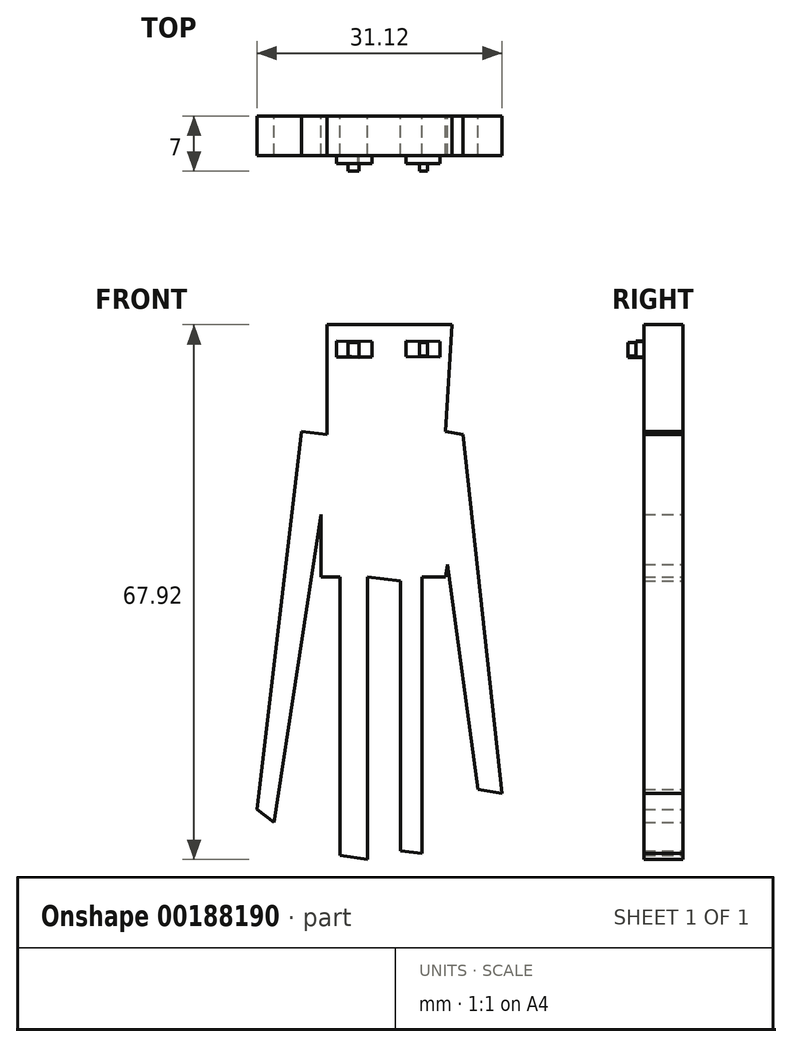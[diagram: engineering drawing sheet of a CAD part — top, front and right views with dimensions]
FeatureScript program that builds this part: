
annotation { "Feature Type Name" : "Feature", "Feature Type Description" : "" }
export const myFeature = defineFeature(function(context is Context, id is Id, definition is map)
    precondition{}
    {
        {
            var Q0;
            Q0=qCreatedBy(makeId("Front.planeOp"),FACE);
            var sketch = newSketch(context, id + "F0", { "sketchPlane" : qUnion([Q0])});
            skLineSegment(sketch, "E0", {"start": v(-12.61, 8.24) * mm, "end": v(-18.23, -39.76) * mm});
            skLineSegment(sketch, "E1", {"start": v(-18.23, -39.76) * mm, "end": v(-16.06, -41.4) * mm});
            skLineSegment(sketch, "E2", {"start": v(-16.06, -41.4) * mm, "end": v(-10.08, -2.27) * mm});
            skLineSegment(sketch, "E3", {"start": v(-10.08, -2.27) * mm, "end": v(-10.08, -10.24) * mm});
            skLineSegment(sketch, "E4", {"start": v(-10.08, -10.24) * mm, "end": v(5.68, -10.24) * mm});
            skLineSegment(sketch, "E5", {"start": v(5.68, -10.24) * mm, "end": v(5.93, -8.62) * mm});
            skLineSegment(sketch, "E6", {"start": v(5.93, -8.62) * mm, "end": v(9.85, -37.23) * mm});
            skLineSegment(sketch, "E7", {"start": v(9.85, -37.23) * mm, "end": v(12.9, -37.7) * mm});
            skLineSegment(sketch, "E8", {"start": v(12.9, -37.7) * mm, "end": v(7.96, 7.9) * mm});
            skLineSegment(sketch, "E9", {"start": v(7.96, 7.9) * mm, "end": v(5.68, 8.24) * mm});
            skLineSegment(sketch, "E10", {"start": v(-9.35, 21.83) * mm, "end": v(-9.35, 7.88) * mm});
            skLineSegment(sketch, "E11", {"start": v(-9.35, 7.88) * mm, "end": v(-12.61, 8.24) * mm});
            skLineSegment(sketch, "E12", {"start": v(-7.72, -10.24) * mm, "end": v(-7.72, -45.56) * mm});
            skLineSegment(sketch, "E13", {"start": v(-7.72, -45.56) * mm, "end": v(-4.23, -46.1) * mm});
            skLineSegment(sketch, "E14", {"start": v(-4.23, -46.1) * mm, "end": v(-4.23, -10.24) * mm});
            skLineSegment(sketch, "E15", {"start": v(-4.23, -10.24) * mm, "end": v(0, -10.73) * mm});
            skLineSegment(sketch, "E16", {"start": v(0, -10.73) * mm, "end": v(0, -45.02) * mm});
            skLineSegment(sketch, "E17", {"start": v(0, -45.02) * mm, "end": v(2.71, -45.33) * mm});
            skLineSegment(sketch, "E18", {"start": v(2.71, -45.33) * mm, "end": v(2.71, -10.24) * mm});
            skLineSegment(sketch, "E19", {"start": v(-9.35, 21.83) * mm, "end": v(6.54, 21.83) * mm});
            skLineSegment(sketch, "E20", {"start": v(6.54, 21.83) * mm, "end": v(5.68, 8.24) * mm});
            skSolve(sketch);
        }
        {
            var Q0;
            Q0 = qSketchRegion(id + "F0", true);
            extrude(context, id + "F1", {"entities" : qUnion([Q0]), "depth" : 5 * mm});
        }
        {
            var Q0;
            Q0=qCreatedBy(makeId("Front.planeOp"),FACE);
            var sketch = newSketch(context, id + "F2", { "sketchPlane" : qUnion([Q0])});
            skLineSegment(sketch, "E21", {"start": v(-8.17, 19.73) * mm, "end": v(-8.17, 17.71) * mm});
            skLineSegment(sketch, "E22", {"start": v(-8.17, 17.71) * mm, "end": v(-3.65, 17.71) * mm});
            skLineSegment(sketch, "E23", {"start": v(-3.65, 17.71) * mm, "end": v(-3.65, 19.69) * mm});
            skLineSegment(sketch, "E24", {"start": v(-3.65, 19.69) * mm, "end": v(-8.17, 19.73) * mm});
            skLineSegment(sketch, "E25", {"start": v(4.99, 19.37) * mm, "end": v(4.99, 17.75) * mm});
            skLineSegment(sketch, "E26", {"start": v(4.99, 17.75) * mm, "end": v(0.67, 17.8) * mm});
            skLineSegment(sketch, "E27", {"start": v(0.67, 17.8) * mm, "end": v(0.67, 19.73) * mm});
            skLineSegment(sketch, "E28", {"start": v(0.67, 19.73) * mm, "end": v(4.99, 19.7) * mm});
            skLineSegment(sketch, "E29", {"start": v(4.99, 19.7) * mm, "end": v(4.99, 17.75) * mm});
            skLineSegment(sketch, "E30", {"start": v(-3.65, 19.69) * mm, "end": v(-3.65, 17.71) * mm});
            skSolve(sketch);
        }
        {
            var Q0;
            Q0 = qSketchRegion(id + "F2", true);
            extrude(context, id + "F3", {"entities" : qUnion([Q0]), "operationType" : NewBodyOperationType.ADD, "depth" : 6 * mm});
        }
        {
            var Q0;
            Q0=qCreatedBy(makeId("Front.planeOp"),FACE);
            var sketch = newSketch(context, id + "F4", { "sketchPlane" : qUnion([Q0])});
            skLineSegment(sketch, "E31", {"start": v(-6.67, 17.84) * mm, "end": v(-6.67, 19.56) * mm});
            skLineSegment(sketch, "E32", {"start": v(-6.67, 19.56) * mm, "end": v(-5.3, 19.56) * mm});
            skLineSegment(sketch, "E33", {"start": v(-5.3, 19.56) * mm, "end": v(-5.3, 17.7) * mm});
            skLineSegment(sketch, "E34", {"start": v(-5.3, 17.7) * mm, "end": v(-6.67, 17.84) * mm});
            skLineSegment(sketch, "E35", {"start": v(2.39, 19.56) * mm, "end": v(2.39, 17.84) * mm});
            skLineSegment(sketch, "E36", {"start": v(2.39, 17.84) * mm, "end": v(3.4, 17.84) * mm});
            skLineSegment(sketch, "E37", {"start": v(3.4, 17.84) * mm, "end": v(3.4, 19.56) * mm});
            skLineSegment(sketch, "E38", {"start": v(3.4, 19.56) * mm, "end": v(2.39, 19.56) * mm});
            skSolve(sketch);
        }
        {
            var Q0;
            Q0 = qSketchRegion(id + "F4", true);
            extrude(context, id + "F5", {"entities" : qUnion([Q0]), "operationType" : NewBodyOperationType.ADD, "depth" : 7 * mm});
        }
    });
